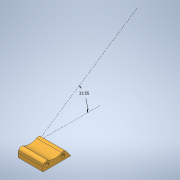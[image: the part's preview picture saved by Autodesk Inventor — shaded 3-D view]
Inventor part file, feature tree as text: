
AUTODESK INVENTOR PART (.ipt)
format: ipt  version: 2020 (Build 240168000, 168)  size: 246,784 bytes
history: native  units: in
note: dims shown in document units (in); Inventor stores cm internally (conversion verified against a paired STEP export)
features: sketch x6, extrude x5, other x3, projected_geometry x3, fillet x2
ambient origin geometry x8: Origin, YZ Plane, XZ Plane, XY Plane, X Axis, Y Axis, Z Axis, Center Point
bodies: Solid1 (feature_tree)
feature tree (19):
  other  "Assembly4.iam"
  other  "Kauri modular session 5 mount.ipt:1"
  other  "session 5.ipt:1"
  extrude  "Extrusion1"  Depth=0.3937in TaperAngle=0.0deg
  extrude  "Extrusion2"  Depth=1.0in TaperAngle=0.0deg
  extrude  "Extrusion3"  Depth=0.3937in TaperAngle=0.0deg
  fillet  "Fillet1"  Radius=0.2362in
  fillet  "Fillet2"  Radius=0.0394in
  extrude  "Extrusion4"  Depth=0.3937in
  extrude  "Extrusion6"  Depth=0.0197in
  sketch  "Sketch7"  dims[d20=0.0197in d23=0.3937in d24=0.0in d25=0.2305in]
  sketch  "Sketch1"  dims[d0=0.3937in d1=1.0in d2=0.0in]
  projected_geometry  "Projected Loop1"
  sketch  "Sketch2"  dims[d3=0.5906in d4=1.0in d5=0.0in]
  sketch  "Sketch3"  dims[d6=0.9843in d7=0.3937in d8=0.0in d9=0.2362in d10=0.0394in]
  projected_geometry  "Projected Loop2"
  sketch  "Sketch4"  dims[d12=0.0197in d15=0.3937in d16=0.0in d17=0.0197in]
  projected_geometry  "Projected Loop3"
  sketch  "Sketch6"  dims[d18=0.0197in d19=0.0197in]
